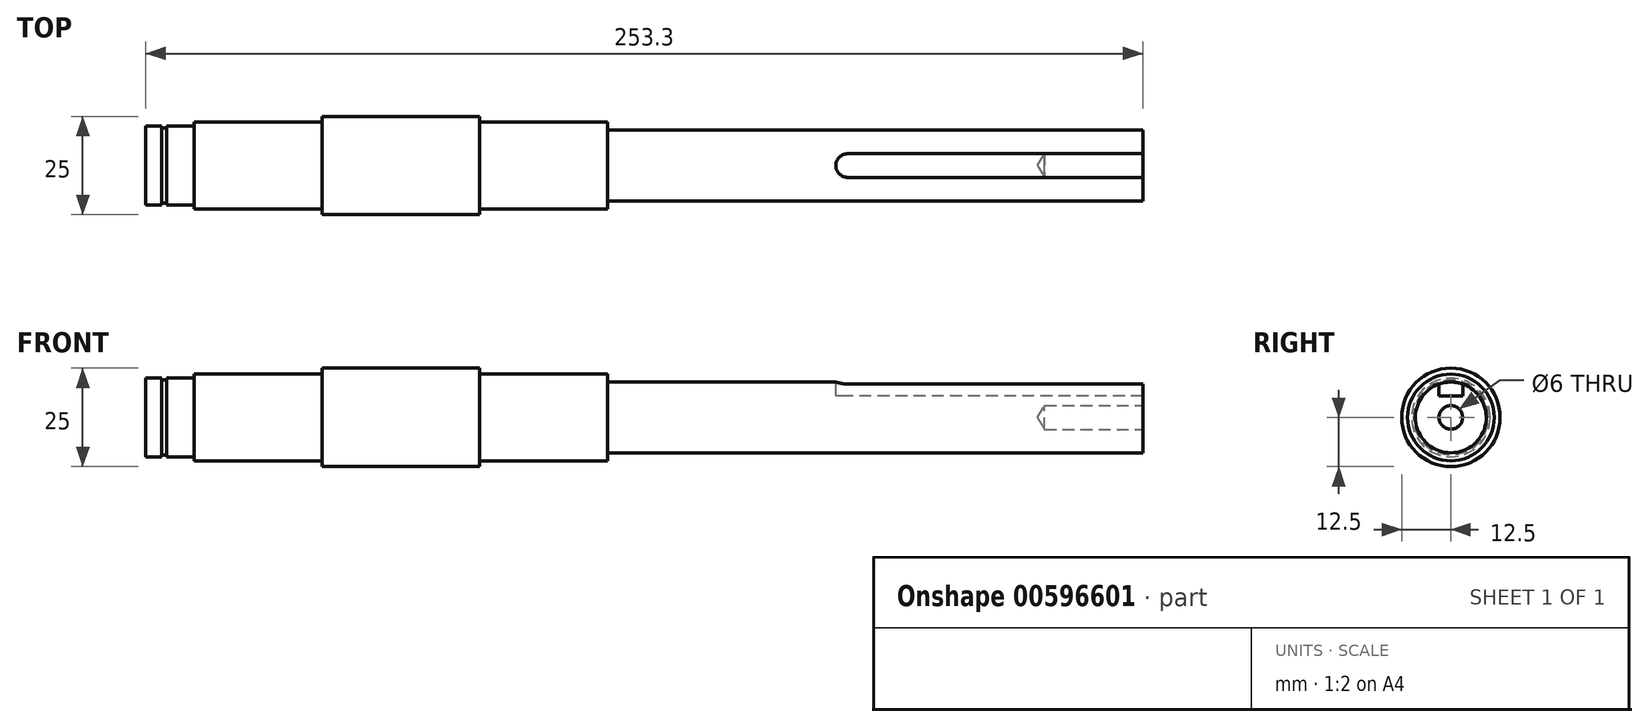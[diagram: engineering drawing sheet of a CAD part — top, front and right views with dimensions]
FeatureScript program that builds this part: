
annotation { "Feature Type Name" : "Feature", "Feature Type Description" : "" }
export const myFeature = defineFeature(function(context is Context, id is Id, definition is map)
    precondition{}
    {
        {
            var Q0;
            Q0=qCreatedBy(makeId("Front.planeOp"),FACE);
            var sketch = newSketch(context, id + "F0", { "sketchPlane" : qUnion([Q0])});
            skLineSegment(sketch, "E0", {"start": v(0, 0) * mm, "end": v(253.3, 0) * mm});
            skLineSegment(sketch, "E1", {"start": v(0, 0) * mm, "end": v(0, 10) * mm});
            skLineSegment(sketch, "E2", {"start": v(0, 10) * mm, "end": v(4, 10) * mm});
            skLineSegment(sketch, "E3", {"start": v(4, 10) * mm, "end": v(4, 9.5) * mm});
            skLineSegment(sketch, "E4", {"start": v(4, 9.5) * mm, "end": v(5.3, 9.5) * mm});
            skLineSegment(sketch, "E5", {"start": v(5.3, 9.5) * mm, "end": v(5.3, 10) * mm});
            skLineSegment(sketch, "E6", {"start": v(5.3, 10) * mm, "end": v(12.3, 10) * mm});
            skLineSegment(sketch, "E7", {"start": v(12.3, 10) * mm, "end": v(12.3, 11) * mm});
            skLineSegment(sketch, "E8", {"start": v(12.3, 11) * mm, "end": v(44.8, 11) * mm});
            skLineSegment(sketch, "E9", {"start": v(44.8, 11) * mm, "end": v(44.8, 12.5) * mm});
            skLineSegment(sketch, "E10", {"start": v(44.8, 12.5) * mm, "end": v(84.8, 12.5) * mm});
            skLineSegment(sketch, "E11", {"start": v(84.8, 12.5) * mm, "end": v(84.8, 11) * mm});
            skLineSegment(sketch, "E12", {"start": v(84.8, 11) * mm, "end": v(117.3, 11) * mm});
            skLineSegment(sketch, "E13", {"start": v(117.3, 11) * mm, "end": v(117.3, 9.5) * mm});
            skLineSegment(sketch, "E14", {"start": v(117.3, 9.5) * mm, "end": v(117.3, 9) * mm});
            skLineSegment(sketch, "E15", {"start": v(117.3, 9) * mm, "end": v(253.3, 9) * mm});
            skLineSegment(sketch, "E16", {"start": v(253.3, 9) * mm, "end": v(253.3, 0) * mm});
            skSolve(sketch);
        }
        {
            var Q0;
            Q0 = qSketchRegion(id + "F0", true);
            var Q1;
            Q1 = qConstructionFilter(qBodyType(qCreatedBy(id + "F0" ,EDGE), BodyType.WIRE), ConstructionObject.NO);
            var Q2;
            Q2=sQuery(id+"F0.wireOp",EDGE,"E0");
            revolve(context, id + "F1", {"entities" : qUnion([Q0]), "surfaceEntities" : qUnion([Q1]), "axis" : qUnion([Q2]), "revolveType" : RevolveType.FULL});
        }
        {
            var Q0;
            Q0=qCreatedBy(makeId("Top.planeOp"),FACE);
            cPlane(context, id + "F2", {"entities" : qUnion([Q0]), "cplaneType" : CPlaneType.OFFSET, "offset" : 9 * mm, "width" : 150 * mm, "height" : 150 * mm});
        }
        {
            var Q0;
            Q0=qCreatedBy(id+"F2.planeOp",FACE);
            var sketch = newSketch(context, id + "F3", { "sketchPlane" : qUnion([Q0])});
            skLineSegment(sketch, "E17", {"start": v(253.3, 0) * mm, "end": v(0, 0) * mm, "construction": true});
            skLineSegment(sketch, "E18.bottom", {"start": v(253.3, -3) * mm, "end": v(178.3, -3) * mm});
            skLineSegment(sketch, "E18.top", {"start": v(253.3, 3) * mm, "end": v(178.3, 3) * mm});
            skLineSegment(sketch, "E18.left", {"start": v(253.3, -3) * mm, "end": v(253.3, 3) * mm});
            skArc(sketch, "E19", {"start": v(178.3, 3) * mm, "mid": v(175.3, 0) * mm, "end": v(178.3, -3) * mm});
            skSolve(sketch);
        }
        {
            var Q0;
            Q0=makeQuery(id+"F3.imprint","IMPRINT",FACE,{"disambiguationData":[TD([[makeQuery(id+"F3.imprint","IMPRINT",EDGE,{"derivedFrom":sQuery(id+"F3.wireOp",EDGE,"E18.bottom")}),-1.0]])]});
            extrude(context, id + "F4", {"entities" : qUnion([Q0]), "operationType" : NewBodyOperationType.REMOVE, "oppositeDirection" : true, "depth" : 3.5 * mm, "offsetDistance" : 25 * mm});
        }
        {
            var Q0;
            Q0=makeQuery(id+"F1.opRevolve","SWEPT_FACE",FACE,{"disambiguationData":[OSD([sQuery(id+"F0.wireOp",EDGE,"E16")])]});
            var sketch = newSketch(context, id + "F5", { "sketchPlane" : qUnion([Q0])});
            skPoint(sketch, "E20", {"position": v(0, 0) * mm});
            skSolve(sketch);
        }
        {
            var Q0;
            Q0=sQuery(id+"F5.wireOp",VERTEX,"E20");
            var Q1;
            Q1=makeQuery(id+"F1.opRevolve","SWEPT_BODY",BODY,{"disambiguationData":[OSD([sQuery(id+"F0.wireOp",EDGE,"E0"),sQuery(id+"F0.wireOp",EDGE,"E1"),sQuery(id+"F0.wireOp",EDGE,"E2"),sQuery(id+"F0.wireOp",EDGE,"E3"),sQuery(id+"F0.wireOp",EDGE,"E4"),sQuery(id+"F0.wireOp",EDGE,"E5"),sQuery(id+"F0.wireOp",EDGE,"E6"),sQuery(id+"F0.wireOp",EDGE,"E7"),sQuery(id+"F0.wireOp",EDGE,"E8"),sQuery(id+"F0.wireOp",EDGE,"E9"),sQuery(id+"F0.wireOp",EDGE,"E10"),sQuery(id+"F0.wireOp",EDGE,"E11"),sQuery(id+"F0.wireOp",EDGE,"E12"),sQuery(id+"F0.wireOp",EDGE,"E13"),sQuery(id+"F0.wireOp",EDGE,"E14"),sQuery(id+"F0.wireOp",EDGE,"E15"),sQuery(id+"F0.wireOp",EDGE,"E16")])]});
            hole(context, id + "F6", {"style" : HoleStyle.SIMPLE, "endStyle" : HoleEndStyle.BLIND, "holeDiameter" : 6 * mm, "majorDiameter" : 5 * mm, "holeDepth" : 25 * mm, "isTappedThrough" : true, "tappedDepth" : 12 * mm, "tapClearance" : 3, "startFromSketch" : true, "locations" : qUnion([Q0]), "scope" : qUnion([Q1])});
        }
    });
